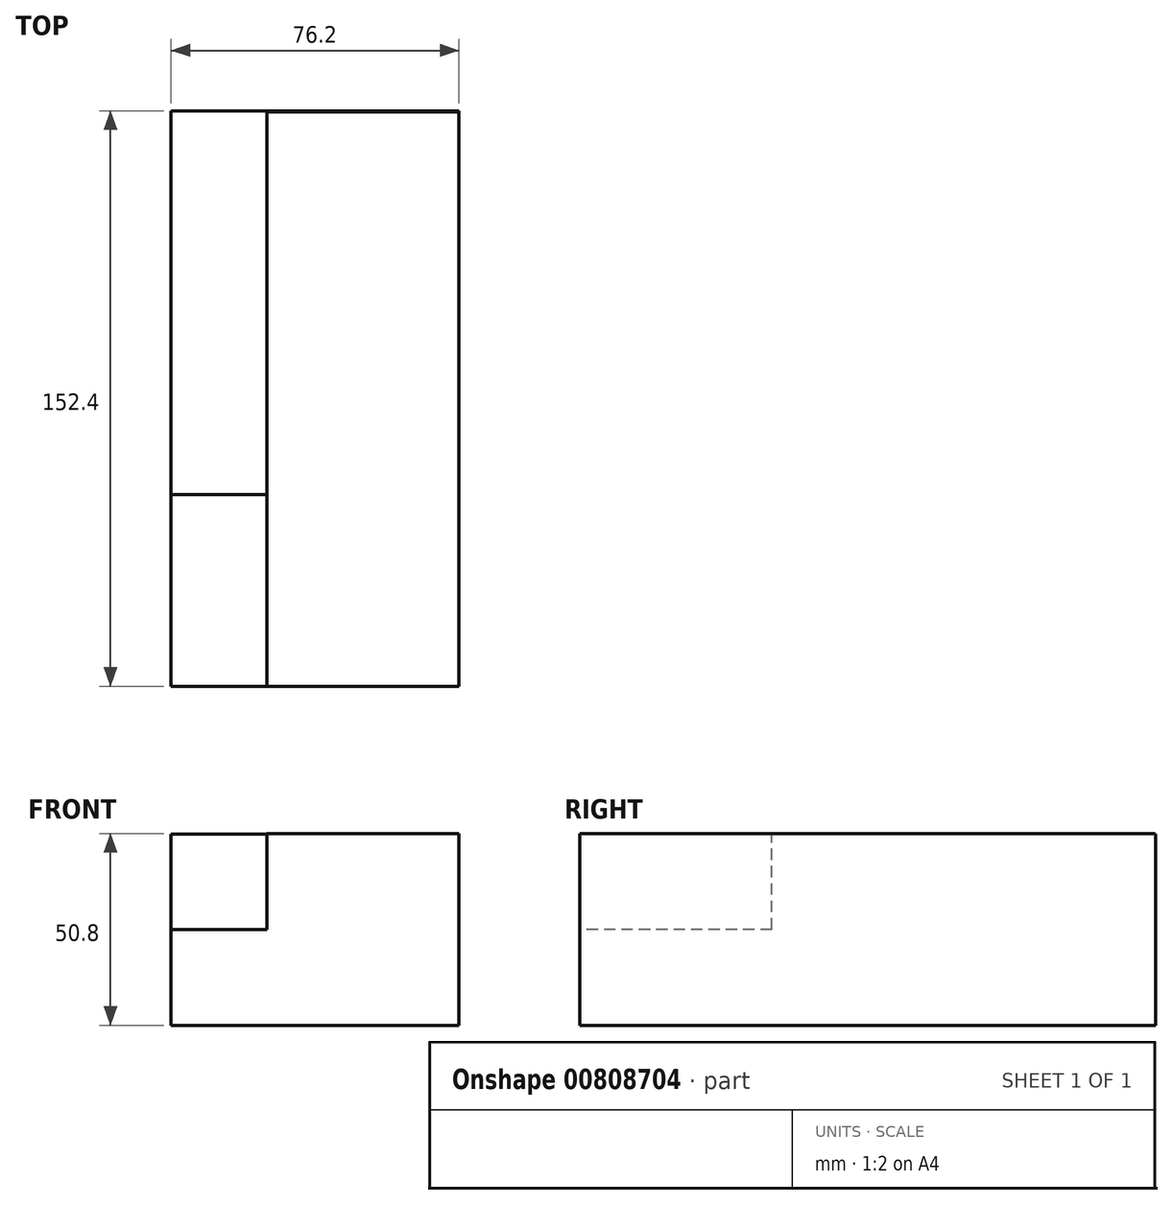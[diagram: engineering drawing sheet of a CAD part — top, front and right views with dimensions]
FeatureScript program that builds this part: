
annotation { "Feature Type Name" : "Feature", "Feature Type Description" : "" }
export const myFeature = defineFeature(function(context is Context, id is Id, definition is map)
    precondition{}
    {
        {
            var Q0;
            Q0=qCreatedBy(makeId("Front.planeOp"),FACE);
            var sketch = newSketch(context, id + "F0", { "sketchPlane" : qUnion([Q0])});
            skLineSegment(sketch, "E0", {"start": v(0, 0) * mm, "end": v(76.2, 0) * mm});
            skLineSegment(sketch, "E1", {"start": v(76.2, 0) * mm, "end": v(76.2, 50.8) * mm});
            skLineSegment(sketch, "E2", {"start": v(76.2, 50.8) * mm, "end": v(25.4, 50.8) * mm});
            skLineSegment(sketch, "E3", {"start": v(25.4, 50.8) * mm, "end": v(25.4, 25.4) * mm});
            skLineSegment(sketch, "E4", {"start": v(25.4, 25.4) * mm, "end": v(0, 25.4) * mm});
            skLineSegment(sketch, "E5", {"start": v(0, 0) * mm, "end": v(0, 25.4) * mm});
            skSolve(sketch);
        }
        {
            var Q0;
            Q0=qCreatedBy(makeId("Right.planeOp"),FACE);
            var sketch = newSketch(context, id + "F1", { "sketchPlane" : qUnion([Q0])});
            skLineSegment(sketch, "E6", {"start": v(0, 25.26) * mm, "end": v(50.8, 25.26) * mm});
            skLineSegment(sketch, "E7", {"start": v(50.8, 25.26) * mm, "end": v(50.8, 50.66) * mm});
            skLineSegment(sketch, "E8", {"start": v(50.8, 50.66) * mm, "end": v(152.4, 50.66) * mm});
            skLineSegment(sketch, "E9", {"start": v(0, 0) * mm, "end": v(152.4, 0) * mm});
            skLineSegment(sketch, "E10", {"start": v(152.4, 50.66) * mm, "end": v(152.4, 0) * mm});
            skLineSegment(sketch, "E11", {"start": v(0, 0) * mm, "end": v(0, 25.26) * mm});
            skSolve(sketch);
        }
        {
            var Q0;
            Q0=makeQuery(id+"F0.imprint","IMPRINT",FACE,{"disambiguationData":[TD([[makeQuery(id+"F0.imprint","IMPRINT",EDGE,{"derivedFrom":sQuery(id+"F0.wireOp",EDGE,"E0")}),1.0]])]});
            extrude(context, id + "F2", {"entities" : qUnion([Q0]), "oppositeDirection" : true, "depth" : 152.15 * mm, "offsetDistance" : 25.4 * mm});
        }
        {
            var Q0;
            Q0=makeQuery(id+"F1.imprint","IMPRINT",FACE,{"disambiguationData":[TD([[makeQuery(id+"F1.imprint","IMPRINT",EDGE,{"derivedFrom":sQuery(id+"F1.wireOp",EDGE,"E6")}),-1.0]])]});
            extrude(context, id + "F3", {"entities" : qUnion([Q0]), "operationType" : NewBodyOperationType.ADD, "depth" : 76.2 * mm, "offsetDistance" : 25.4 * mm});
        }
    });
